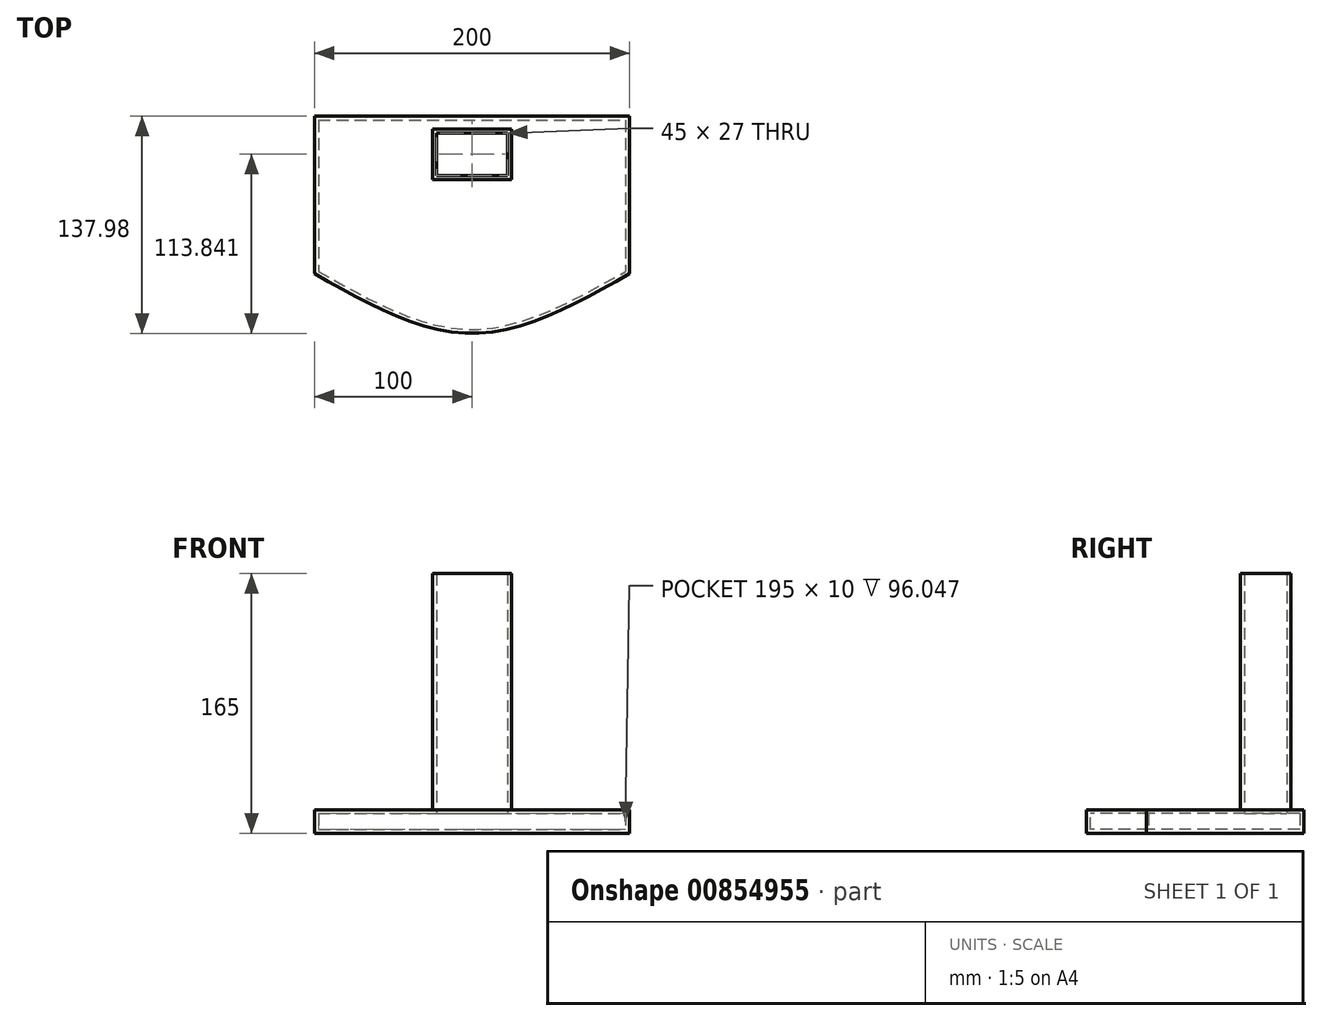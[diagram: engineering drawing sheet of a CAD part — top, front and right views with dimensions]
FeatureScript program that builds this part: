
annotation { "Feature Type Name" : "Feature", "Feature Type Description" : "" }
export const myFeature = defineFeature(function(context is Context, id is Id, definition is map)
    precondition{}
    {
        {
            var Q0;
            Q0=qCreatedBy(makeId("Top.planeOp"),FACE);
            var sketch = newSketch(context, id + "F0", { "sketchPlane" : qUnion([Q0])});
            skLineSegment(sketch, "E0.bottom", {"start": v(-100, 50) * mm, "end": v(100, 50) * mm});
            skLineSegment(sketch, "E0.left", {"start": v(-100, 50) * mm, "end": v(-100, -50) * mm});
            skLineSegment(sketch, "E0.right", {"start": v(100, 50) * mm, "end": v(100, -50) * mm});
            skFitSpline(sketch, "E1", {"points": [v(-100, -50) * mm, v(0, -87.98) * mm, v(100, -50) * mm], "startDerivative": vector(200, -113.94) * mm, "endDerivative": vector(200, 113.94) * mm});
            skSolve(sketch);
        }
        {
            var Q0;
            Q0=makeQuery(id+"F0.imprint","IMPRINT",FACE,{"disambiguationData":[TD([[makeQuery(id+"F0.imprint","IMPRINT",EDGE,{"derivedFrom":sQuery(id+"F0.wireOp",EDGE,"E0.bottom")}),-1.0]])]});
            extrude(context, id + "F1", {"entities" : qUnion([Q0]), "depth" : 15 * mm, "offsetDistance" : 25 * mm});
        }
        {
            var Q0;
            Q0=makeQuery(id+"F1.opExtrude","CAP_FACE",FACE,{"disambiguationData":[OSD([sQuery(id+"F0.wireOp",EDGE,"E0.bottom"),sQuery(id+"F0.wireOp",EDGE,"E0.left"),sQuery(id+"F0.wireOp",EDGE,"E0.right"),sQuery(id+"F0.wireOp",EDGE,"E1")])],"isStart":false});
            var sketch = newSketch(context, id + "F2", { "sketchPlane" : qUnion([Q0])});
            skLineSegment(sketch, "E2.bottom", {"start": v(-25, 9.86) * mm, "end": v(25, 9.86) * mm});
            skLineSegment(sketch, "E2.top", {"start": v(-25, 41.86) * mm, "end": v(25, 41.86) * mm});
            skLineSegment(sketch, "E2.left", {"start": v(-25, 9.86) * mm, "end": v(-25, 41.86) * mm});
            skLineSegment(sketch, "E2.right", {"start": v(25, 9.86) * mm, "end": v(25, 41.86) * mm});
            skPoint(sketch, "E2.middle", {"position": v(0, 25.86) * mm});
            skSolve(sketch);
        }
        {
            var Q0;
            Q0=makeQuery(id+"F2.imprint","IMPRINT",FACE,{"disambiguationData":[TD([[makeQuery(id+"F2.imprint","IMPRINT",EDGE,{"derivedFrom":sQuery(id+"F2.wireOp",EDGE,"E2.bottom")}),1.0]])]});
            extrude(context, id + "F3", {"entities" : qUnion([Q0]), "operationType" : NewBodyOperationType.ADD, "depth" : 150 * mm, "offsetDistance" : 25 * mm});
        }
        {
            var Q0;
            Q0=makeQuery(id+"F3.opExtrude","CAP_FACE",FACE,{"disambiguationData":[OSD([sQuery(id+"F2.wireOp",EDGE,"E2.bottom"),sQuery(id+"F2.wireOp",EDGE,"E2.top"),sQuery(id+"F2.wireOp",EDGE,"E2.left"),sQuery(id+"F2.wireOp",EDGE,"E2.right")])],"isStart":false});
            shell(context, id + "F4", {"entities" : qUnion([Q0]), "thickness" : 2.5 * mm});
        }
    });
